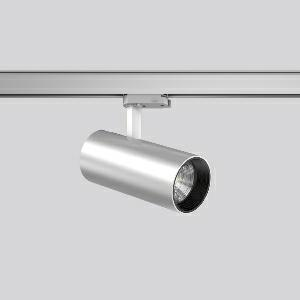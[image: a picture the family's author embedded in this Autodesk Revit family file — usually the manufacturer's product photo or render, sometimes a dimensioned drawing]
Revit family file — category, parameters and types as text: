
# Revit family: deecos_s_mini_742198_004_3_76_cef9
name_source: partatom
category: Lighting Fixtures
units: mm (PartAtom-declared; Revit-internal decimal feet)

## family parameters
Cut with Voids When Loaded = No
Host = Face
Light Source = No
Part Type = Normal
Room Calculation Point = No
Round Connector Dimension = Use Diameter
Shared = No

## types (1)
- DEECOS S mini (1 x LED Modul 935, 2250 lm, 3500)
    Apparent Load = 20 VA
    Approval mark = CE
    CIE Flux Codes = 99 100 100 100 100
    Color Rendering = 92
    Color Temperature = 3500
    Default Elevation = 1800 mm
    Description = Series: DEECOS S mini
LED surface-mounted projector in modern design with no visible cooling ribs. Housing: die-cast aluminium, powder-coated. Rotation range: 356°. Swivel range: 90°. Black plastic ring and recessed LED to prevent glare from the side. Optical assembly with lens made of plastic (polycarbonate) for the best homogeneous light distribution - can be changed without tools. Best colour rendering index Ra>90. With adapter for RZB 3-circuit DALI tracks. Suitable for Track on ceiling, Wall track. High quality converter without flickering and stroboscopic effect. The following accessories can be mounted without use of tools: interchangeable lenses, decorative glasses, honeycomb louvre, clear and frosted diffusers, white interchangeable plastic ring. 
Colour: silver
Diameter: 87 mm
Height: 214 mm
Lamp: LED
Socket: without socket
Colour temperature: 3500K
Colour rendering index (CRI): 92
System power: 20 W
Rated luminous flux: 2250 lm
Luminous efficiency: 113 lm/W
Control gear: Converter, dimmable, DALI
Protection class: I
Type of protection: IP 20
    Height = 214 mm
    Lamp = 1 x LED Modul 935
    Lamp Light Flux = 2250 lm
    Lamp count = 1
    Length = 87 mm
    Lifetime = 50000 h
    Luminous efficacy = 113 lm/W
    Manufacturer = RZB
    ModVariant = No
    Model = 742198.004.3.76
    Mounting Place = Ceiling
    Mounting Type = Rail mounted
    Number of Poles = 1
    OnlyDefault = Yes
    Power Factor = 1
    Product Name = DEECOS S mini
    Product group = Track mounted projectors
    ProductGroupID = 301
    Protection Class = Protection class I
    Protection Degree = IP 20
    RLX_Detail_Level = 1
    RLX_Emergency_Light_Flux = 0 lm
    RLX_Emergency_Type = 0
    RLX_Emergency_Type_DB = No
    RlxData = <blob elided: 37261 chars, md5=6f1bf491>
    Socket = socket
    Standby Power = 0 W
    System Light Flux = 2250 lm
    System Power = 20 W
    Type Comments = Product without accessories
    Type Image = 741930.004.jpg
    URL = http://relux.com
    VarID = ---
    Voltage = 230 V
    Voltage Range = 220-240 V
    Weight = 0.00 kg
    Width = 0 mm  [stored 0 ft]

note: [stored X ft] marks values corroborated as IEEE doubles in the binary element streams (Revit-internal decimal feet)

## geometry (parser evidence)
native form markers: Blend x4, Sweep x12
no freeform markers — native parametric forms only
